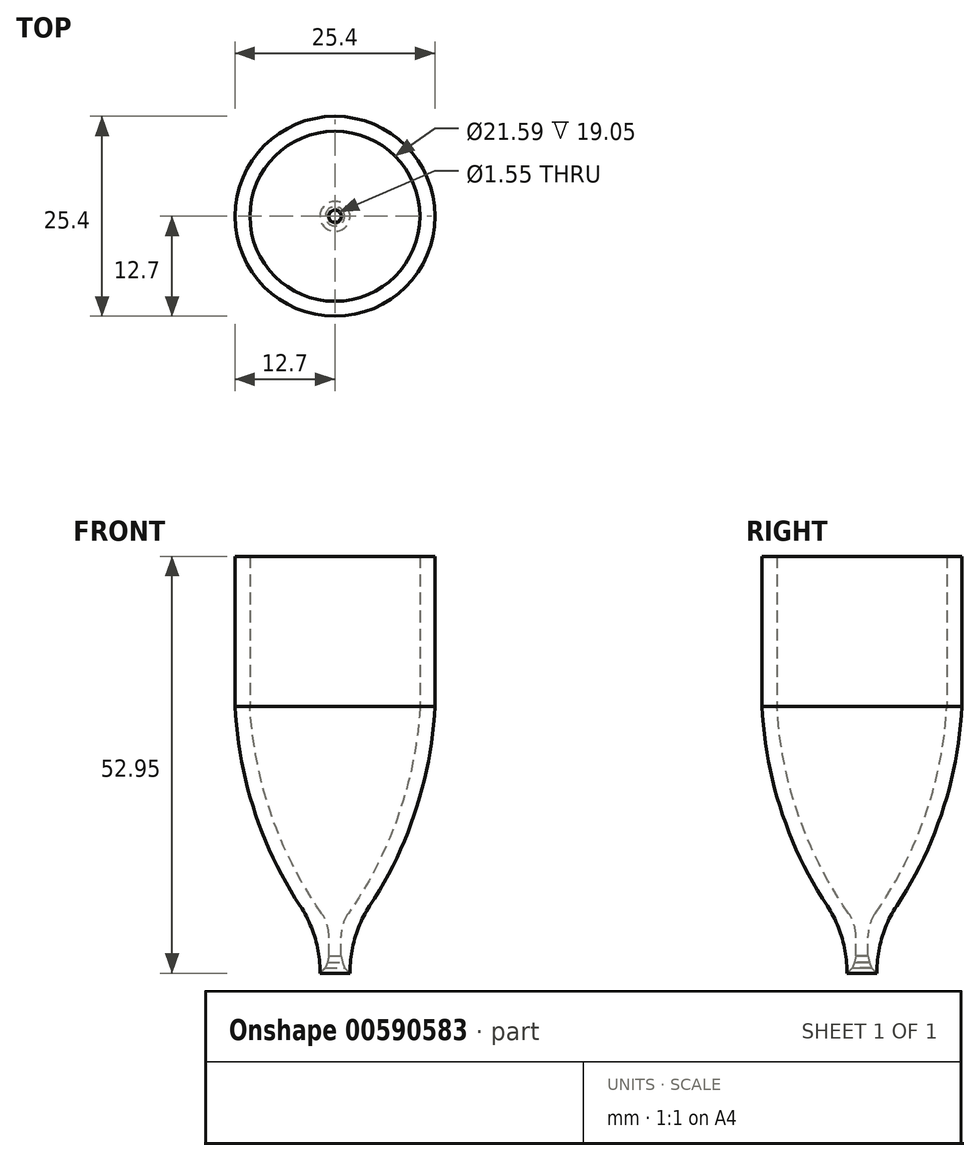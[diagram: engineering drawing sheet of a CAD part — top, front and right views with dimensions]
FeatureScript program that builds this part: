
annotation { "Feature Type Name" : "Feature", "Feature Type Description" : "" }
export const myFeature = defineFeature(function(context is Context, id is Id, definition is map)
    precondition{}
    {
        {
            var Q0;
            Q0=qCreatedBy(makeId("Top.planeOp"),FACE);
            var sketch = newSketch(context, id + "F0", { "sketchPlane" : qUnion([Q0])});
            skCircle(sketch, "E0", {"center": v(0, 0) * mm, "radius": 10.8 * mm});
            skCircle(sketch, "E1", {"center": v(0, 0) * mm, "radius": 12.7 * mm});
            skSolve(sketch);
        }
        {
            var Q0;
            Q0=makeQuery(id+"F0.imprint","IMPRINT",FACE,{"disambiguationData":[TD([[makeQuery(id+"F0.imprint","IMPRINT",EDGE,{"derivedFrom":sQuery(id+"F0.wireOp",EDGE,"E0")}),-1.0]])]});
            extrude(context, id + "F1", {"entities" : qUnion([Q0]), "depth" : 19.05 * mm, "offsetDistance" : 25.4 * mm});
        }
        {
            var Q0;
            Q0=qCreatedBy(makeId("Front.planeOp"),FACE);
            var sketch = newSketch(context, id + "F2", { "sketchPlane" : qUnion([Q0])});
            skLineSegment(sketch, "E2", {"start": v(0, 0) * mm, "end": v(12.7, 0) * mm});
            skLineSegment(sketch, "E3", {"start": v(0, 0) * mm, "end": v(0, -24.39) * mm});
            skLineSegment(sketch, "E4", {"start": v(0, -24.39) * mm, "end": v(4.03, -24.39) * mm});
            skArc(sketch, "E5", {"start": v(4.03, -24.39) * mm, "mid": v(9.94, -12.75) * mm, "end": v(12.7, 0) * mm});
            skLineSegment(sketch, "E6", {"start": v(12.7, 0) * mm, "end": v(10.8, 0) * mm});
            skLineSegment(sketch, "E7", {"start": v(4.03, -24.39) * mm, "end": v(2.13, -24.39) * mm});
            skArc(sketch, "E8", {"start": v(2.13, -24.39) * mm, "mid": v(8.04, -12.75) * mm, "end": v(10.8, 0) * mm});
            skLineSegment(sketch, "E9", {"start": v(0, 0) * mm, "end": v(0, -27.56) * mm});
            skPoint(sketch, "E9.endSnap0", {"position": v(0, -12.2) * mm});
            skLineSegment(sketch, "E10", {"start": v(0, -27.56) * mm, "end": v(4.87, -27.56) * mm});
            skArc(sketch, "E11", {"start": v(2.88, -27.56) * mm, "mid": v(9.82, -14.5) * mm, "end": v(12.7, 0) * mm});
            skArc(sketch, "E12", {"start": v(0.78, -27.56) * mm, "mid": v(7.82, -14.52) * mm, "end": v(10.8, 0) * mm});
            skSolve(sketch);
        }
        {
            var Q0;
            Q0=makeQuery(id+"F1.opExtrude","CAP_FACE",FACE,{"disambiguationData":[OSD([sQuery(id+"F0.wireOp",EDGE,"E0"),sQuery(id+"F0.wireOp",EDGE,"E1")])],"isStart":false});
            var sketch = newSketch(context, id + "F3", { "sketchPlane" : qUnion([Q0])});
            skCircle(sketch, "E13", {"center": v(0, 0) * mm, "radius": 0.95 * mm});
            skCircle(sketch, "E14", {"center": v(0, 0) * mm, "radius": 0.64 * mm});
            skSolve(sketch);
        }
        {
            var Q0;
            Q0=makeQuery(id+"F3.imprint","IMPRINT",FACE,{"disambiguationData":[TD([[makeQuery(id+"F3.imprint","IMPRINT",EDGE,{"derivedFrom":sQuery(id+"F3.wireOp",EDGE,"E14")}),1.0]])]});
            extrude(context, id + "F4", {"entities" : qUnion([Q0]), "operationType" : NewBodyOperationType.REMOVE, "endBound" : BoundingType.THROUGH_ALL, "oppositeDirection" : true, "depth" : 76.2 * mm, "offsetDistance" : 25.4 * mm});
        }
        {
            var Q0;
            {var subQ0=sQuery(id+"F2.wireOp",EDGE,"E5");Q0=makeQuery(id+"F2.imprint","IMPRINT",FACE,{"disambiguationData":[TD([[makeQuery(id+"F2.imprint","IMPRINT",EDGE,{"derivedFrom":subQ0}),1.0]])]});}
            var Q1;
            {var subQ5=sQuery(id+"F2.wireOp",EDGE,"E5");Q1=makeQuery(id+"F2.imprint","IMPRINT",FACE,{"disambiguationData":[TD([[makeQuery(id+"F2.imprint","IMPRINT",EDGE,{"derivedFrom":subQ5}),-1.0]])]});}
            var Q2;
            Q2=sQuery(id+"F2.wireOp",EDGE,"E9");
            revolve(context, id + "F5", {"operationType" : NewBodyOperationType.ADD, "entities" : qUnion([Q0, Q1]), "axis" : qUnion([Q2]), "revolveType" : RevolveType.FULL});
        }
        {
            var Q0;
            Q0=makeQuery(id+"F5.opRevolve","SWEPT_EDGE",EDGE,{"disambiguationData":[OSD([sQuery(id+"F2.wireOp",EDGE,"E10"),sQuery(id+"F2.wireOp",EDGE,"E11")])]});
            fillet(context, id + "F6", {"entities" : qUnion([Q0]), "radius" : 1.9 * mm, "tangentPropagation" : true, "allowEdgeOverflow" : false});
        }
        {
            var Q0;
            Q0=makeQuery(id+"F5.opRevolve","SWEPT_FACE",FACE,{"disambiguationData":[OSD([sQuery(id+"F2.wireOp",EDGE,"E10")])]});
            extrude(context, id + "F7", {"entities" : qUnion([Q0]), "operationType" : NewBodyOperationType.ADD, "depth" : 6.35 * mm, "offsetDistance" : 25.4 * mm});
        }
        {
            var Q0;
            Q0=makeQuery(id+"F7.opExtrude","CAP_EDGE",EDGE,{"disambiguationData":[OSD([sQuery(id+"F2.wireOp",EDGE,"E10"),sQuery(id+"F2.wireOp",EDGE,"E12")])],"isStart":false});
            chamfer(context, id + "F8", {"entities" : qUnion([Q0]), "width" : 1.14 * mm, "tangentPropagation" : true});
        }
        {
            var Q0;
            {var subQ0=sQuery(id+"F2.wireOp",EDGE,"E12");var subQ1=sQuery(id+"F2.wireOp",EDGE,"E10");Q0=makeQuery(id+"F8.opChamfer","BLEND_EDGE",EDGE,{"blendedFrom":[makeQuery(id+"F7.opExtrude","CAP_EDGE",EDGE,{"disambiguationData":[OSD([subQ1,subQ0])],"isStart":false}),makeQuery(id+"F7.opExtrude","SWEPT_FACE",FACE,{"disambiguationData":[OSD([subQ1,subQ0])]})],"blendedInto":[makeQuery(id+"F7.opExtrude","SWEPT_FACE",FACE,{"disambiguationData":[OSD([subQ1,subQ0])]})]});}
            chamfer(context, id + "F9", {"entities" : qUnion([Q0]), "width" : 1.56 * mm, "tangentPropagation" : true});
        }
        {
            var Q0;
            {var subQ0=sQuery(id+"F2.wireOp",EDGE,"E12");var subQ1=sQuery(id+"F2.wireOp",EDGE,"E10");var subQ2=makeQuery(id+"F7.opExtrude","SWEPT_FACE",FACE,{"disambiguationData":[OSD([subQ1,subQ0])]});Q0=makeQuery(id+"F9.opChamfer","BLEND_EDGE",EDGE,{"blendedFrom":[makeQuery(id+"F8.opChamfer","BLEND_EDGE",EDGE,{"blendedFrom":[makeQuery(id+"F7.opExtrude","CAP_EDGE",EDGE,{"disambiguationData":[OSD([subQ1,subQ0])],"isStart":false}),subQ2],"blendedInto":[subQ2]}),subQ2],"blendedInto":[subQ2]});}
            chamfer(context, id + "F10", {"entities" : qUnion([Q0]), "width" : 2.18 * mm, "tangentPropagation" : true});
        }
        {
            var Q0;
            {var subQ0=sQuery(id+"F2.wireOp",EDGE,"E11");var subQ1=sQuery(id+"F2.wireOp",EDGE,"E10");Q0=makeQuery(id+"F7.boolean.opBoolean","MERGE",EDGE,{"derivedFrom":[makeQuery(id+"F6.opFillet","BLEND_EDGE",EDGE,{"blendedFrom":[makeQuery(id+"F5.opRevolve","SWEPT_EDGE",EDGE,{"disambiguationData":[OSD([subQ1,subQ0])]}),makeQuery(id+"F5.opRevolve","SWEPT_FACE",FACE,{"disambiguationData":[OSD([subQ1])]})],"blendedInto":[makeQuery(id+"F5.opRevolve","SWEPT_FACE",FACE,{"disambiguationData":[OSD([subQ1])]})]}),makeQuery(id+"F7.opExtrude","CAP_EDGE",EDGE,{"disambiguationData":[OSD([subQ1,subQ0])],"isStart":true})]});}
            fillet(context, id + "F11", {"entities" : qUnion([Q0]), "radius" : 15.24 * mm, "tangentPropagation" : true, "allowEdgeOverflow" : false});
        }
        {
            var Q0;
            {var subQ0=sQuery(id+"F2.wireOp",EDGE,"E12");var subQ1=sQuery(id+"F2.wireOp",EDGE,"E10");Q0=makeQuery(id+"F7.boolean.opBoolean","MERGE",EDGE,{"derivedFrom":[makeQuery(id+"F5.opRevolve","SWEPT_EDGE",EDGE,{"disambiguationData":[OSD([subQ1,subQ0])]}),makeQuery(id+"F7.opExtrude","CAP_EDGE",EDGE,{"disambiguationData":[OSD([subQ1,subQ0])],"isStart":true})]});}
            fillet(context, id + "F12", {"entities" : qUnion([Q0]), "radius" : 5.08 * mm, "tangentPropagation" : true, "allowEdgeOverflow" : false});
        }
    });
